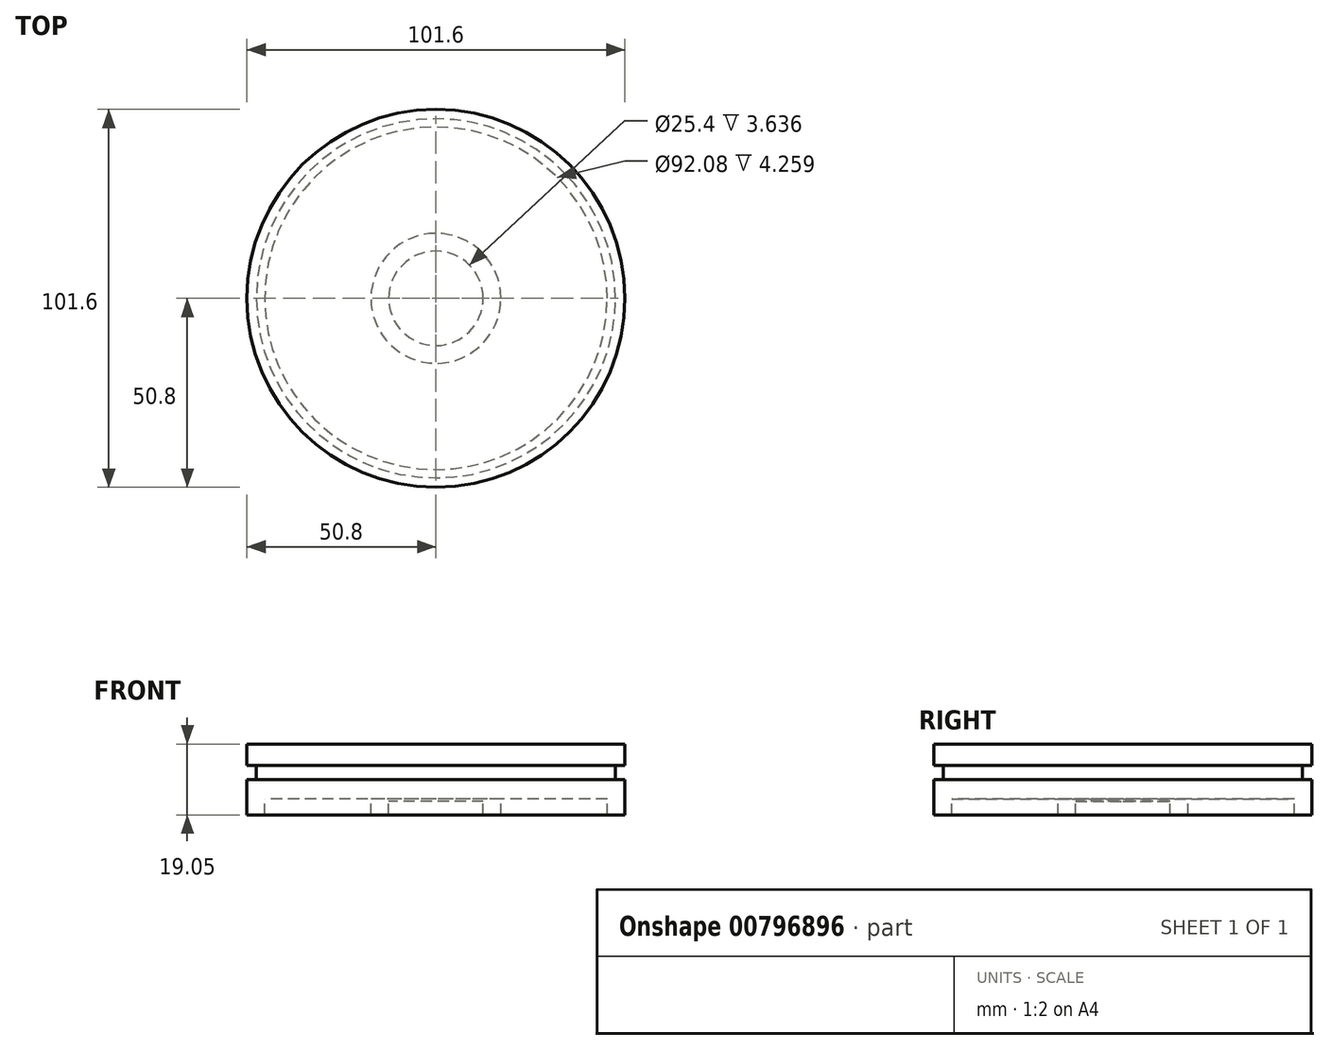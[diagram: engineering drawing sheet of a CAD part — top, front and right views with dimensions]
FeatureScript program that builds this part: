
annotation { "Feature Type Name" : "Feature", "Feature Type Description" : "" }
export const myFeature = defineFeature(function(context is Context, id is Id, definition is map)
    precondition{}
    {
        {
            var Q0;
            Q0=qCreatedBy(makeId("Front.planeOp"),FACE);
            var sketch = newSketch(context, id + "F0", { "sketchPlane" : qUnion([Q0])});
            skLineSegment(sketch, "E0", {"start": v(0, 3.64) * mm, "end": v(12.7, 3.64) * mm});
            skLineSegment(sketch, "E1", {"start": v(12.7, 3.64) * mm, "end": v(12.7, 0) * mm});
            skLineSegment(sketch, "E2", {"start": v(12.7, 0) * mm, "end": v(17.46, 0) * mm});
            skLineSegment(sketch, "E3", {"start": v(17.46, 0) * mm, "end": v(17.46, 4.26) * mm});
            skLineSegment(sketch, "E4", {"start": v(17.46, 4.26) * mm, "end": v(46.04, 4.26) * mm});
            skLineSegment(sketch, "E5", {"start": v(46.04, 4.26) * mm, "end": v(46.04, 0) * mm});
            skLineSegment(sketch, "E6", {"start": v(46.04, 0) * mm, "end": v(50.8, 0) * mm});
            skLineSegment(sketch, "E7", {"start": v(50.8, 19.05) * mm, "end": v(0, 19.05) * mm});
            skLineSegment(sketch, "E8", {"start": v(0, 19.05) * mm, "end": v(0, 3.64) * mm});
            skLineSegment(sketch, "E9", {"start": v(50.8, 19.05) * mm, "end": v(50.8, 13.33) * mm});
            skLineSegment(sketch, "E10", {"start": v(50.8, 13.33) * mm, "end": v(48.26, 13.33) * mm});
            skLineSegment(sketch, "E11", {"start": v(48.26, 13.33) * mm, "end": v(48.26, 9.53) * mm});
            skLineSegment(sketch, "E12", {"start": v(48.26, 9.53) * mm, "end": v(50.8, 9.53) * mm});
            skLineSegment(sketch, "E13", {"start": v(50.8, 9.53) * mm, "end": v(50.8, 0) * mm});
            skSolve(sketch);
        }
        {
            var Q0;
            Q0=makeQuery(id+"F0.imprint","IMPRINT",FACE,{"disambiguationData":[TD([[makeQuery(id+"F0.imprint","IMPRINT",EDGE,{"derivedFrom":sQuery(id+"F0.wireOp",EDGE,"E0")}),1.0]])]});
            var Q1;
            Q1=sQuery(id+"F0.wireOp",EDGE,"E8");
            revolve(context, id + "F1", {"surfaceOperationType" : NewSurfaceOperationType.NEW, "entities" : qUnion([Q0]), "axis" : qUnion([Q1]), "revolveType" : RevolveType.FULL});
        }
    });
